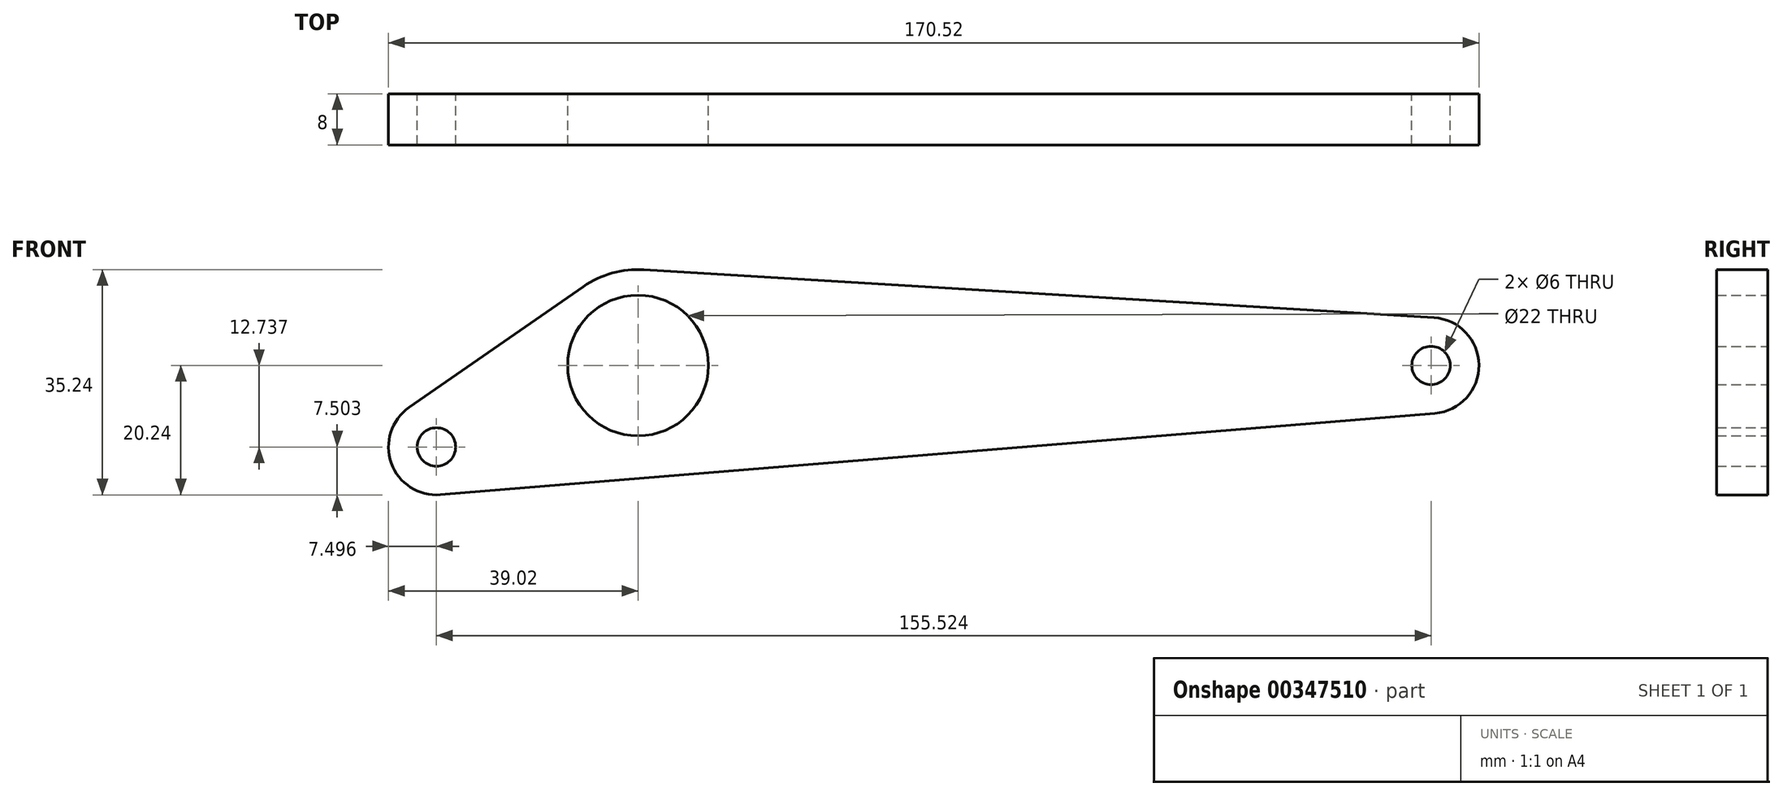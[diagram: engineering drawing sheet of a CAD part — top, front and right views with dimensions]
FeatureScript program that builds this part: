
annotation { "Feature Type Name" : "Feature", "Feature Type Description" : "" }
export const myFeature = defineFeature(function(context is Context, id is Id, definition is map)
    precondition{}
    {
        {
            assignVariable(context, id + "F0", {"name" : "Epaisseur", "anyValue" : 8});
        }
        {
            var Q0;
            Q0=qCreatedBy(makeId("Front.planeOp"),FACE);
            var sketch = newSketch(context, id + "F1", { "sketchPlane" : qUnion([Q0])});
            skCircle(sketch, "E0", {"center": v(0, 0) * mm, "radius": 11 * mm});
            skCircle(sketch, "E1", {"center": v(124, 0) * mm, "radius": 3 * mm});
            skArc(sketch, "E2", {"start": v(124.61, -7.47) * mm, "mid": v(131.5, 0.08) * mm, "end": v(124.45, 7.49) * mm});
            skArc(sketch, "E3", {"start": v(0.9, 14.97) * mm, "mid": v(-4.04, 14.44) * mm, "end": v(-8.55, 12.33) * mm});
            skCircle(sketch, "E4", {"center": v(-31.52, -12.74) * mm, "radius": 3 * mm});
            skLineSegment(sketch, "E5", {"start": v(-31.52, -12.74) * mm, "end": v(0, 0) * mm, "construction": true});
            skLineSegment(sketch, "E6", {"start": v(0, 0) * mm, "end": v(124, 0) * mm, "construction": true});
            skArc(sketch, "E7", {"start": v(-35.8, -6.57) * mm, "mid": v(-38.58, -15.27) * mm, "end": v(-30.91, -20.21) * mm});
            skLineSegment(sketch, "E8", {"start": v(-35.8, -6.57) * mm, "end": v(-8.55, 12.33) * mm});
            skLineSegment(sketch, "E9", {"start": v(0.9, 14.97) * mm, "end": v(124.45, 7.49) * mm});
            skLineSegment(sketch, "E10", {"start": v(124.61, -7.47) * mm, "end": v(-30.91, -20.21) * mm});
            skSolve(sketch);
        }
        {
            var Q0;
            Q0=makeQuery(id+"F1.imprint","IMPRINT",FACE,{"disambiguationData":[TD([[makeQuery(id+"F1.imprint","IMPRINT",EDGE,{"derivedFrom":sQuery(id+"F1.wireOp",EDGE,"E0")}),-1.0]])]});
            extrude(context, id + "F2", {"entities" : qUnion([Q0]), "depth" : (getVariable(context, 'Epaisseur')) * mm, "symmetric" : true});
        }
    });
